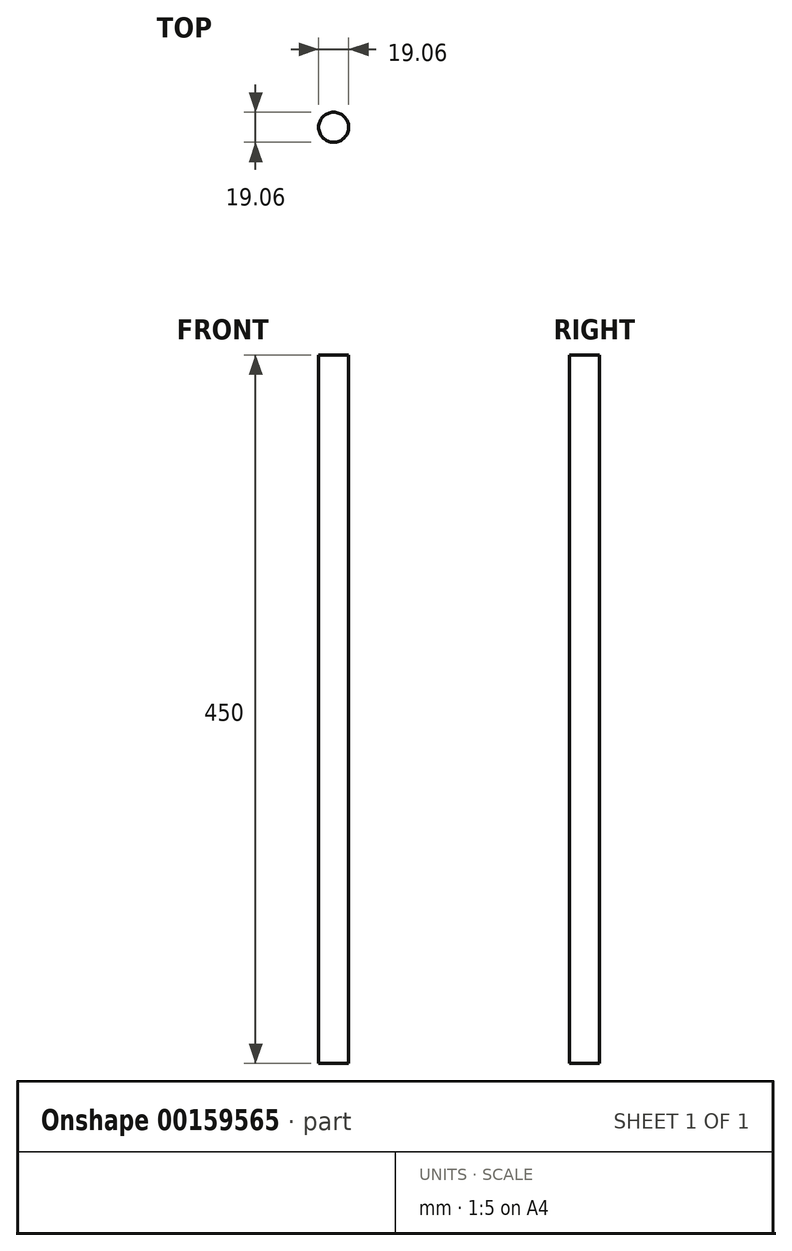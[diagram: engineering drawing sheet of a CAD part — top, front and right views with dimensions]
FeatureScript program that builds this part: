
annotation { "Feature Type Name" : "Feature", "Feature Type Description" : "" }
export const myFeature = defineFeature(function(context is Context, id is Id, definition is map)
    precondition{}
    {
        {
            var Q0;
            Q0=qCreatedBy(makeId("Top.planeOp"),FACE);
            var sketch = newSketch(context, id + "F0", { "sketchPlane" : qUnion([Q0])});
            skCircle(sketch, "E0", {"center": v(0, 0) * mm, "radius": 9.53 * mm});
            skSolve(sketch);
        }
        {
            var Q0;
            Q0 = qSketchRegion(id + "F0", true);
            extrude(context, id + "F1", {"entities" : qUnion([Q0]), "depth" : 450 * mm});
        }
    });
